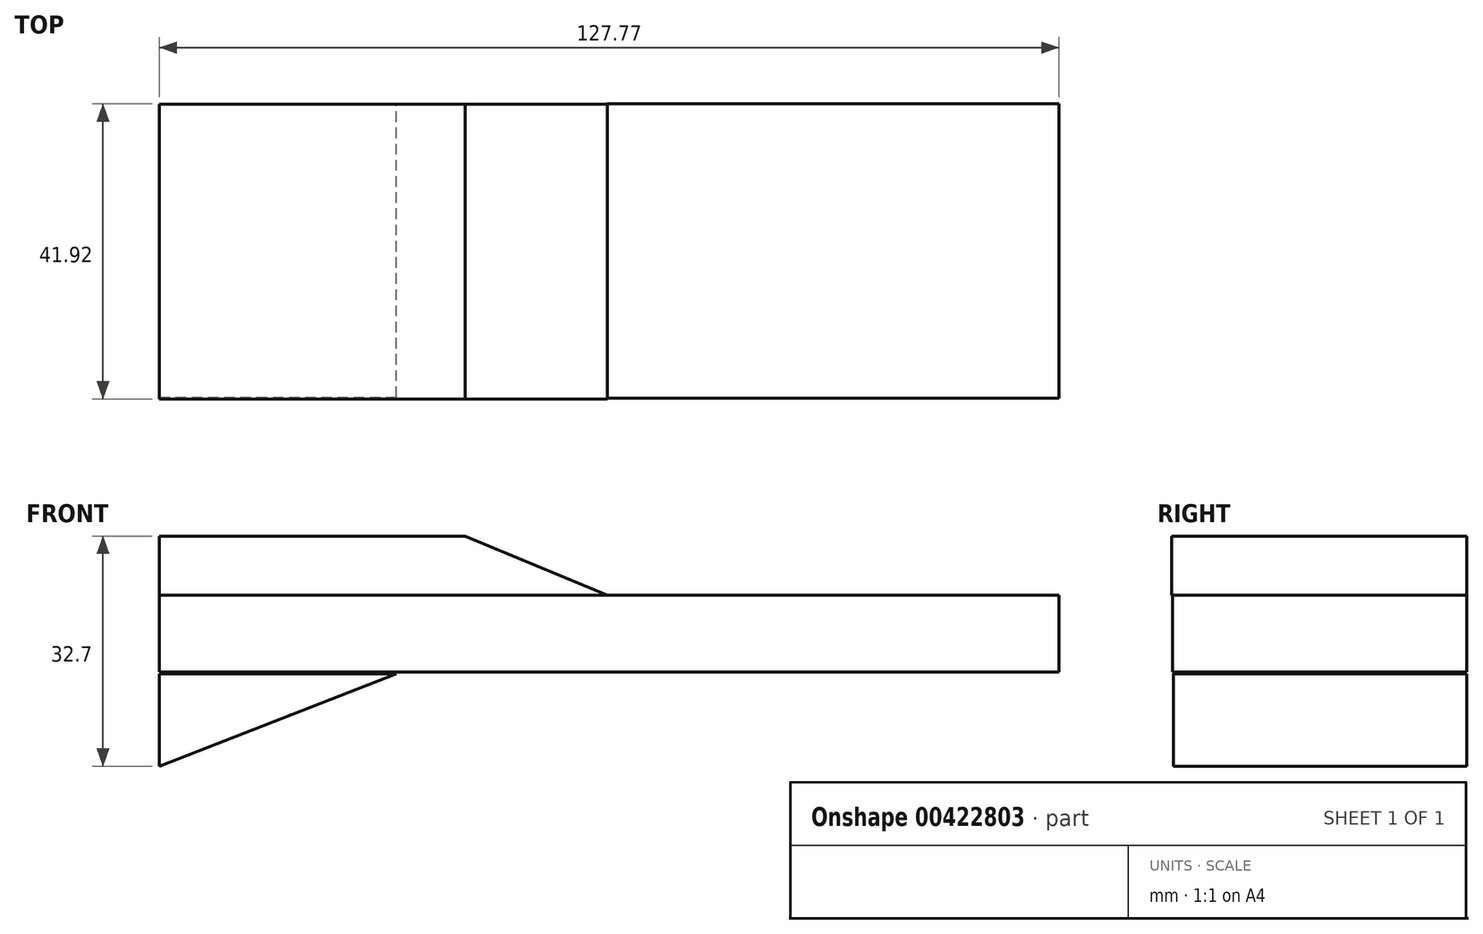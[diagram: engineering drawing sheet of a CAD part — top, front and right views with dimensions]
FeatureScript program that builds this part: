
annotation { "Feature Type Name" : "Feature", "Feature Type Description" : "" }
export const myFeature = defineFeature(function(context is Context, id is Id, definition is map)
    precondition{}
    {
        {
            var Q0;
            Q0=qCreatedBy(makeId("Front.planeOp"),FACE);
            var sketch = newSketch(context, id + "F0", { "sketchPlane" : qUnion([Q0])});
            skLineSegment(sketch, "E0", {"start": v(0, -11.22) * mm, "end": v(0, -24.32) * mm});
            skLineSegment(sketch, "E1", {"start": v(0, -11.22) * mm, "end": v(33.67, -11.22) * mm});
            skLineSegment(sketch, "E2", {"start": v(0, -24.32) * mm, "end": v(33.67, -11.22) * mm});
            skSolve(sketch);
        }
        {
            var Q0;
            Q0=qCreatedBy(makeId("Top.planeOp"),FACE);
            var sketch = newSketch(context, id + "F1", { "sketchPlane" : qUnion([Q0])});
            skLineSegment(sketch, "E3.bottom", {"start": v(0, 21.85) * mm, "end": v(127.77, 21.85) * mm});
            skLineSegment(sketch, "E3.top", {"start": v(0, -19.95) * mm, "end": v(127.77, -19.95) * mm});
            skLineSegment(sketch, "E3.left", {"start": v(0, 21.85) * mm, "end": v(0, -19.95) * mm});
            skLineSegment(sketch, "E3.right", {"start": v(127.77, 21.85) * mm, "end": v(127.77, -19.95) * mm});
            skSolve(sketch);
        }
        {
            var Q0;
            Q0=makeQuery(id+"F1.imprint","IMPRINT",FACE,{"disambiguationData":[TD([[makeQuery(id+"F1.imprint","IMPRINT",EDGE,{"derivedFrom":sQuery(id+"F1.wireOp",EDGE,"E3.bottom")}),-1.0]])]});
            extrude(context, id + "F2", {"entities" : qUnion([Q0]), "oppositeDirection" : true, "depth" : 10.92 * mm});
        }
        {
            var Q0;
            Q0=makeQuery(id+"F0.imprint","IMPRINT",FACE,{"disambiguationData":[TD([[makeQuery(id+"F0.imprint","IMPRINT",EDGE,{"derivedFrom":sQuery(id+"F0.wireOp",EDGE,"E0")}),1.0]])]});
            extrude(context, id + "F3", {"entities" : qUnion([Q0]), "depth" : 19.8 * mm});
        }
        {
            var Q0;
            Q0=makeQuery(id+"F3.opExtrude","CAP_FACE",FACE,{"disambiguationData":[OSD([sQuery(id+"F0.wireOp",EDGE,"E0"),sQuery(id+"F0.wireOp",EDGE,"E1"),sQuery(id+"F0.wireOp",EDGE,"E2")])],"isStart":true});
            extrude(context, id + "F4", {"entities" : qUnion([Q0]), "operationType" : NewBodyOperationType.ADD, "depth" : 21.84 * mm});
        }
        {
            var Q0;
            Q0=qCreatedBy(makeId("Front.planeOp"),FACE);
            var sketch = newSketch(context, id + "F5", { "sketchPlane" : qUnion([Q0])});
            skLineSegment(sketch, "E4", {"start": v(63.63, 0) * mm, "end": v(43.4, 8.38) * mm});
            skLineSegment(sketch, "E5", {"start": v(43.4, 8.38) * mm, "end": v(0, 8.38) * mm});
            skLineSegment(sketch, "E6", {"start": v(0, 8.38) * mm, "end": v(0, 0) * mm});
            skLineSegment(sketch, "E7", {"start": v(0, 0) * mm, "end": v(63.63, 0) * mm});
            skSolve(sketch);
        }
        {
            var Q0;
            Q0=makeQuery(id+"F5.imprint","IMPRINT",FACE,{"disambiguationData":[TD([[makeQuery(id+"F5.imprint","IMPRINT",EDGE,{"derivedFrom":sQuery(id+"F5.wireOp",EDGE,"E4")}),1.0]])]});
            extrude(context, id + "F6", {"entities" : qUnion([Q0]), "operationType" : NewBodyOperationType.ADD, "depth" : 20.07 * mm});
        }
        {
            var Q0;
            Q0=makeQuery(id+"F6.opExtrude","CAP_FACE",FACE,{"disambiguationData":[OSD([sQuery(id+"F5.wireOp",EDGE,"E4"),sQuery(id+"F5.wireOp",EDGE,"E5"),sQuery(id+"F5.wireOp",EDGE,"E6"),sQuery(id+"F5.wireOp",EDGE,"E7")])],"isStart":true});
            extrude(context, id + "F7", {"entities" : qUnion([Q0]), "operationType" : NewBodyOperationType.ADD, "depth" : 21.84 * mm});
        }
        {
            var Q0;
            Q0=qCreatedBy(makeId("Front.planeOp"),FACE);
            var sketch = newSketch(context, id + "F8", { "sketchPlane" : qUnion([Q0])});
            skLineSegment(sketch, "E8", {"start": v(64.12, -11.34) * mm, "end": v(64.12, -31.07) * mm});
            skLineSegment(sketch, "E9", {"start": v(76.45, -11.34) * mm, "end": v(76.45, -54.26) * mm});
            skSolve(sketch);
        }
        {
            var Q0;
            Q0=sQuery(id+"F8.wireOp",EDGE,"E8");
            var Q1;
            Q1=sQuery(id+"F8.wireOp",EDGE,"E9");
            revolve(context, id + "F9", {"bodyType" : ToolBodyType.SURFACE, "surfaceEntities" : qUnion([Q0]), "axis" : qUnion([Q1]), "revolveType" : RevolveType.FULL});
        }
        {
            var Q0;
            Q0=qCreatedBy(makeId("Front.planeOp"),FACE);
            var sketch = newSketch(context, id + "F10", { "sketchPlane" : qUnion([Q0])});
            skLineSegment(sketch, "E10", {"start": v(72.01, -31.57) * mm, "end": v(72.01, -66.59) * mm});
            skLineSegment(sketch, "E11", {"start": v(76.45, -31.57) * mm, "end": v(76.45, -88.78) * mm});
            skSolve(sketch);
        }
        {
            var Q0;
            Q0=sQuery(id+"F10.wireOp",EDGE,"E10");
            var Q1;
            Q1=sQuery(id+"F10.wireOp",EDGE,"E11");
            revolve(context, id + "F11", {"bodyType" : ToolBodyType.SURFACE, "surfaceEntities" : qUnion([Q0]), "axis" : qUnion([Q1]), "revolveType" : RevolveType.FULL});
        }
    });
